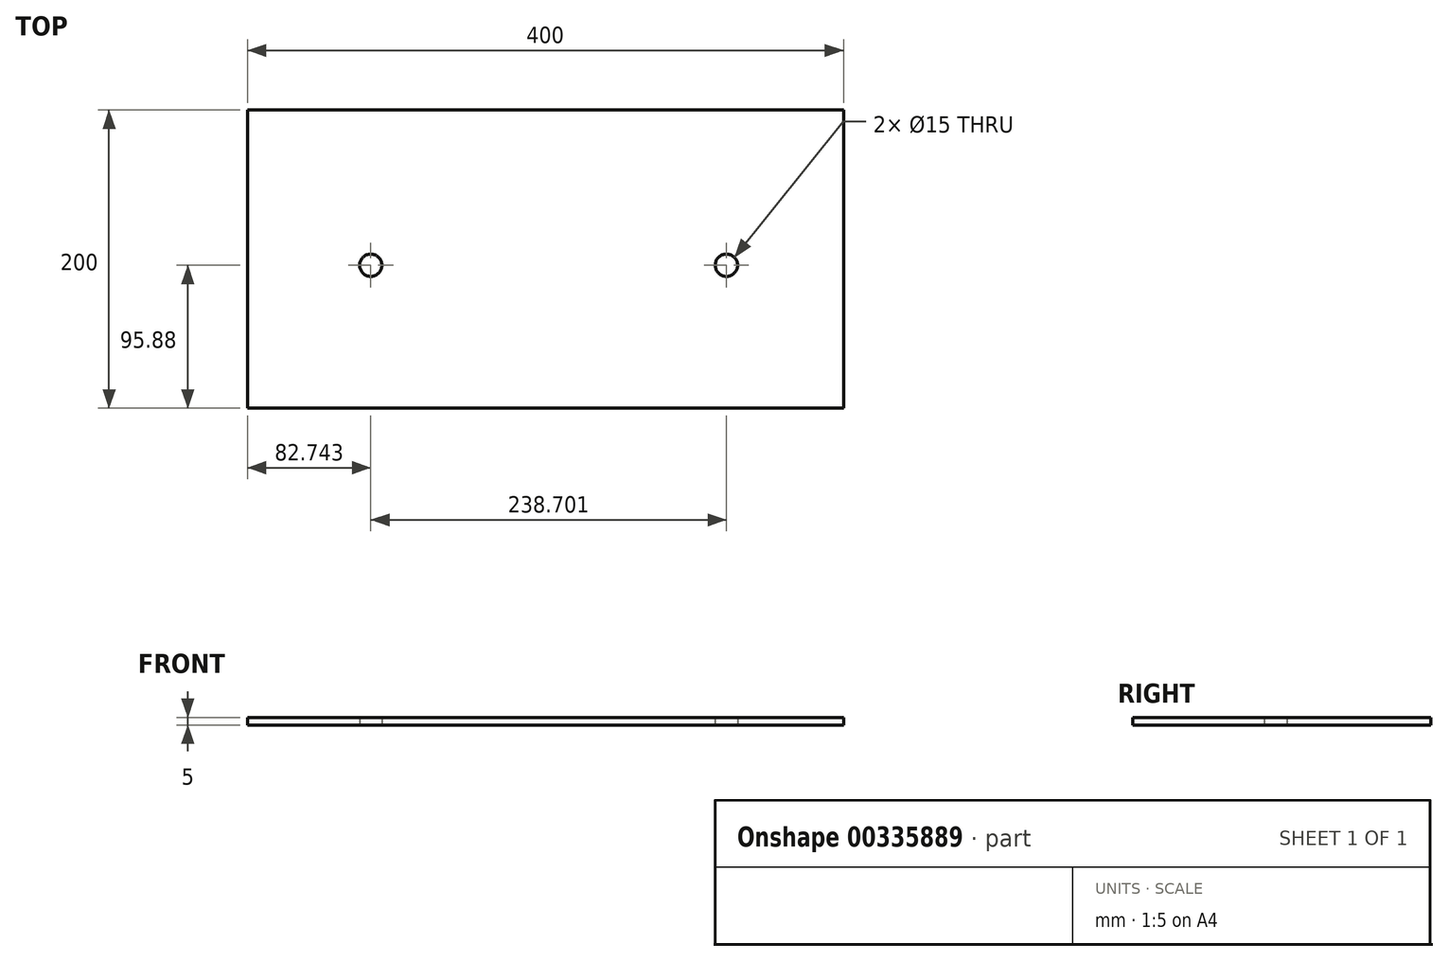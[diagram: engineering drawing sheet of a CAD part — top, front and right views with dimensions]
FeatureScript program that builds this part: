
annotation { "Feature Type Name" : "Feature", "Feature Type Description" : "" }
export const myFeature = defineFeature(function(context is Context, id is Id, definition is map)
    precondition{}
    {
        {
            var Q0;
            Q0=qCreatedBy(makeId("Top.planeOp"),FACE);
            var sketch = newSketch(context, id + "F0", { "sketchPlane" : qUnion([Q0])});
            skLineSegment(sketch, "E0.bottom", {"start": v(-199.77, 104.12) * mm, "end": v(200.23, 104.12) * mm});
            skLineSegment(sketch, "E0.top", {"start": v(-199.77, -95.88) * mm, "end": v(200.23, -95.88) * mm});
            skLineSegment(sketch, "E0.left", {"start": v(-199.77, 104.12) * mm, "end": v(-199.77, -95.88) * mm});
            skLineSegment(sketch, "E0.right", {"start": v(200.23, 104.12) * mm, "end": v(200.23, -95.88) * mm});
            skSolve(sketch);
        }
        {
            var Q0;
            Q0=makeQuery(id+"F0.imprint","IMPRINT",FACE,{"disambiguationData":[TD([[makeQuery(id+"F0.imprint","IMPRINT",EDGE,{"derivedFrom":sQuery(id+"F0.wireOp",EDGE,"E0.bottom")}),-1.0]])]});
            extrude(context, id + "F1", {"entities" : qUnion([Q0]), "depth" : 5 * mm});
        }
        {
            var Q0;
            Q0=qCreatedBy(makeId("Top.planeOp"),FACE);
            var sketch = newSketch(context, id + "F2", { "sketchPlane" : qUnion([Q0])});
            skCircle(sketch, "E1", {"center": v(121.67, 0) * mm, "radius": 7.5 * mm});
            skSolve(sketch);
        }
        {
            var Q0;
            Q0 = qSketchRegion(id + "F2", true);
            extrude(context, id + "F3", {"entities" : qUnion([Q0]), "depth" : 25 * mm});
        }
        {
            var Q0;
            Q0=makeQuery(id+"F3.opExtrude","SWEPT_BODY",BODY,{"disambiguationData":[OSD([sQuery(id+"F2.wireOp",EDGE,"E1")])]});
            var Q1;
            Q1=makeQuery(id+"F1.opExtrude","SWEPT_BODY",BODY,{"disambiguationData":[OSD([sQuery(id+"F0.wireOp",EDGE,"E0.bottom"),sQuery(id+"F0.wireOp",EDGE,"E0.top"),sQuery(id+"F0.wireOp",EDGE,"E0.left"),sQuery(id+"F0.wireOp",EDGE,"E0.right")])]});
            booleanBodies(context, id + "F4", {"operationType" : BooleanOperationType.SUBTRACTION, "tools" : qUnion([Q0]), "targets" : qUnion([Q1])});
        }
        {
            var Q0;
            Q0=qCreatedBy(makeId("Top.planeOp"),FACE);
            var sketch = newSketch(context, id + "F5", { "sketchPlane" : qUnion([Q0])});
            skCircle(sketch, "E2", {"center": v(-117.03, 0) * mm, "radius": 7.5 * mm});
            skSolve(sketch);
        }
        {
            var Q0;
            Q0 = qSketchRegion(id + "F5", true);
            extrude(context, id + "F6", {"entities" : qUnion([Q0]), "depth" : 25 * mm});
        }
        {
            var Q0;
            Q0=makeQuery(id+"F6.opExtrude","SWEPT_BODY",BODY,{"disambiguationData":[OSD([sQuery(id+"F5.wireOp",EDGE,"E2")])]});
            var Q1;
            Q1=makeQuery(id+"F1.opExtrude","SWEPT_BODY",BODY,{"disambiguationData":[OSD([sQuery(id+"F0.wireOp",EDGE,"E0.bottom"),sQuery(id+"F0.wireOp",EDGE,"E0.top"),sQuery(id+"F0.wireOp",EDGE,"E0.left"),sQuery(id+"F0.wireOp",EDGE,"E0.right")])]});
            booleanBodies(context, id + "F7", {"operationType" : BooleanOperationType.SUBTRACTION, "tools" : qUnion([Q0]), "targets" : qUnion([Q1])});
        }
    });
